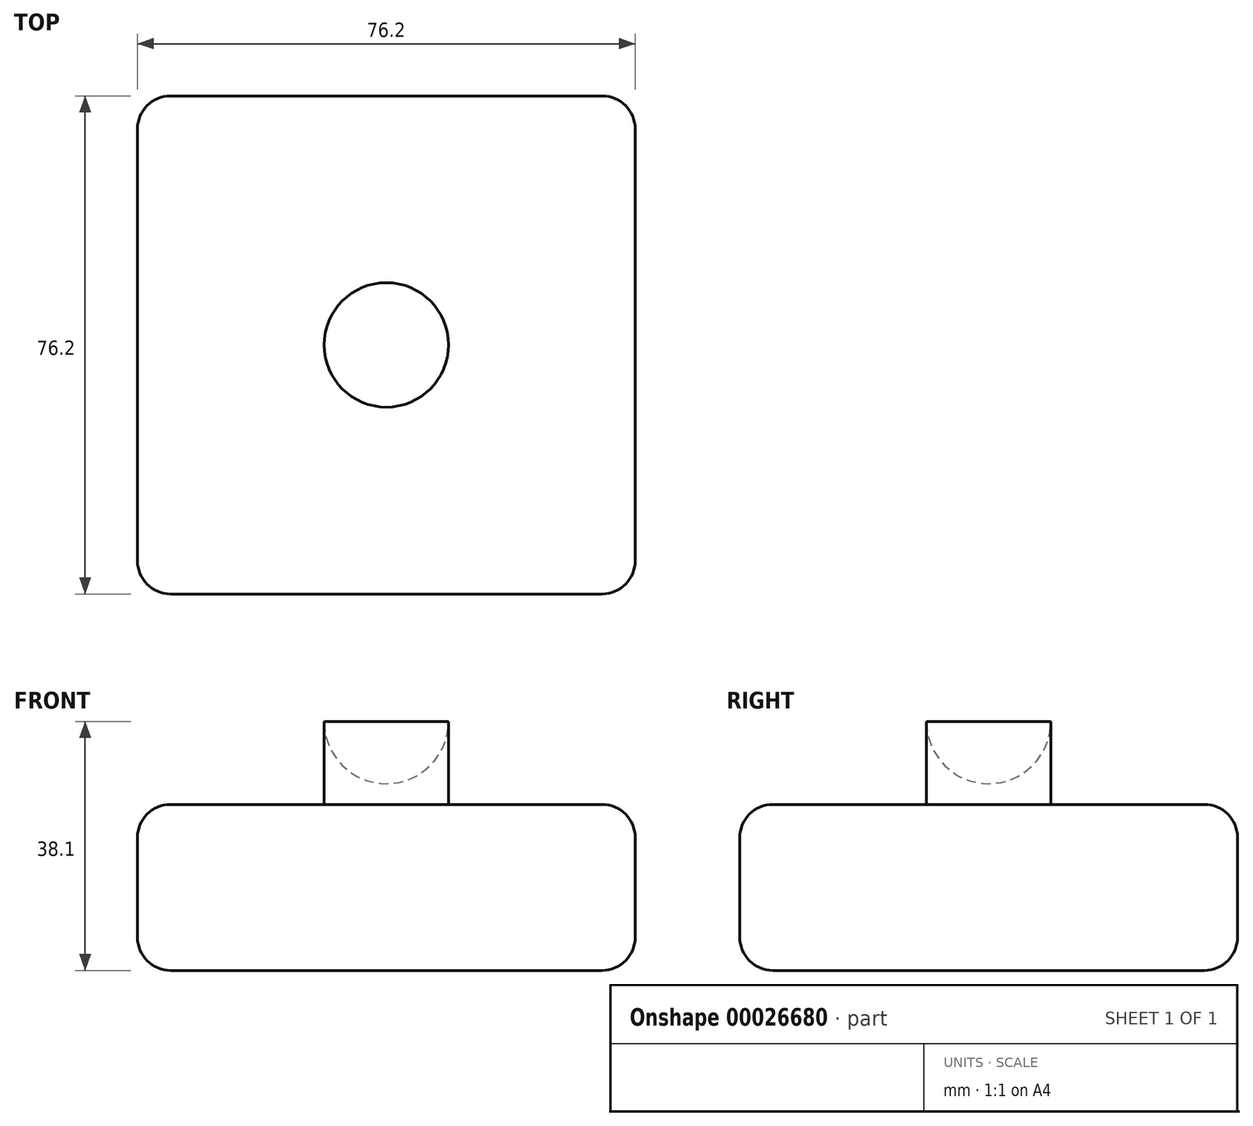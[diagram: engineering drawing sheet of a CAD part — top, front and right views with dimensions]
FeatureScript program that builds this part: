
annotation { "Feature Type Name" : "Feature", "Feature Type Description" : "" }
export const myFeature = defineFeature(function(context is Context, id is Id, definition is map)
    precondition{}
    {
        {
            var Q0;
            Q0=qCreatedBy(makeId("Top.planeOp"),FACE);
            var sketch = newSketch(context, id + "F0", { "sketchPlane" : qUnion([Q0])});
            skLineSegment(sketch, "E0.rect.bottom", {"start": v(-38.1, 38.1) * mm, "end": v(38.1, 38.1) * mm});
            skLineSegment(sketch, "E0.rect.top", {"start": v(-38.1, -38.1) * mm, "end": v(38.1, -38.1) * mm});
            skLineSegment(sketch, "E0.rect.left", {"start": v(-38.1, 38.1) * mm, "end": v(-38.1, -38.1) * mm});
            skLineSegment(sketch, "E0.rect.right", {"start": v(38.1, 38.1) * mm, "end": v(38.1, -38.1) * mm});
            skPoint(sketch, "E0.rect.middle", {"position": v(0, 0) * mm});
            skSolve(sketch);
        }
        {
            var Q0;
            Q0=makeQuery(id+"F0.imprint","IMPRINT",FACE,{"disambiguationData":[TD([[makeQuery(id+"F0.imprint","IMPRINT",EDGE,{"derivedFrom":sQuery(id+"F0.wireOp",EDGE,"E0.rect.bottom")}),-1.0]])]});
            extrude(context, id + "F1", {"entities" : qUnion([Q0]), "depth" : 25.4 * mm});
        }
        {
            var Q0;
            Q0=makeQuery(id+"F1.opExtrude","CAP_EDGE",EDGE,{"disambiguationData":[OSD([sQuery(id+"F0.wireOp",EDGE,"E0.rect.top")])],"isStart":true});
            var Q1;
            Q1=makeQuery(id+"F1.opExtrude","CAP_EDGE",EDGE,{"disambiguationData":[OSD([sQuery(id+"F0.wireOp",EDGE,"E0.rect.right")])],"isStart":true});
            var Q2;
            Q2=makeQuery(id+"F1.opExtrude","CAP_EDGE",EDGE,{"disambiguationData":[OSD([sQuery(id+"F0.wireOp",EDGE,"E0.rect.bottom")])],"isStart":true});
            var Q3;
            Q3=makeQuery(id+"F1.opExtrude","CAP_EDGE",EDGE,{"disambiguationData":[OSD([sQuery(id+"F0.wireOp",EDGE,"E0.rect.left")])],"isStart":true});
            var Q4;
            Q4=makeQuery(id+"F1.opExtrude","CAP_EDGE",EDGE,{"disambiguationData":[OSD([sQuery(id+"F0.wireOp",EDGE,"E0.rect.top")])],"isStart":false});
            var Q5;
            Q5=makeQuery(id+"F1.opExtrude","CAP_EDGE",EDGE,{"disambiguationData":[OSD([sQuery(id+"F0.wireOp",EDGE,"E0.rect.left")])],"isStart":false});
            var Q6;
            Q6=makeQuery(id+"F1.opExtrude","SWEPT_EDGE",EDGE,{"disambiguationData":[OSD([sQuery(id+"F0.wireOp",EDGE,"E0.rect.top"),sQuery(id+"F0.wireOp",EDGE,"E0.rect.left")])]});
            var Q7;
            Q7=makeQuery(id+"F1.opExtrude","SWEPT_EDGE",EDGE,{"disambiguationData":[OSD([sQuery(id+"F0.wireOp",EDGE,"E0.rect.bottom"),sQuery(id+"F0.wireOp",EDGE,"E0.rect.left")])]});
            var Q8;
            Q8=makeQuery(id+"F1.opExtrude","SWEPT_FACE",FACE,{"disambiguationData":[OSD([sQuery(id+"F0.wireOp",EDGE,"E0.rect.bottom")])]});
            var Q9;
            Q9=makeQuery(id+"F1.opExtrude","CAP_EDGE",EDGE,{"disambiguationData":[OSD([sQuery(id+"F0.wireOp",EDGE,"E0.rect.right")])],"isStart":false});
            var Q10;
            Q10=makeQuery(id+"F1.opExtrude","SWEPT_EDGE",EDGE,{"disambiguationData":[OSD([sQuery(id+"F0.wireOp",EDGE,"E0.rect.top"),sQuery(id+"F0.wireOp",EDGE,"E0.rect.right")])]});
            fillet(context, id + "F2", {"entities" : qUnion([Q0, Q1, Q2, Q3, Q4, Q5, Q6, Q7, Q8, Q9, Q10]), "radius" : 5.08 * mm, "tangentPropagation" : true, "allowEdgeOverflow" : false});
        }
        {
            var Q0;
            Q0=makeQuery(id+"F1.opExtrude","CAP_FACE",FACE,{"disambiguationData":[OSD([sQuery(id+"F0.wireOp",EDGE,"E0.rect.bottom"),sQuery(id+"F0.wireOp",EDGE,"E0.rect.top"),sQuery(id+"F0.wireOp",EDGE,"E0.rect.left"),sQuery(id+"F0.wireOp",EDGE,"E0.rect.right")])],"isStart":false});
            var sketch = newSketch(context, id + "F3", { "sketchPlane" : qUnion([Q0])});
            skCircle(sketch, "E1", {"center": v(0, 0) * mm, "radius": 9.53 * mm});
            skSolve(sketch);
        }
        {
            var Q0;
            Q0=makeQuery(id+"F3.imprint","IMPRINT",FACE,{"disambiguationData":[TD([[makeQuery(id+"F3.imprint","IMPRINT",EDGE,{"derivedFrom":sQuery(id+"F3.wireOp",EDGE,"E1")}),1.0]])]});
            extrude(context, id + "F4", {"entities" : qUnion([Q0]), "operationType" : NewBodyOperationType.ADD, "depth" : 12.7 * mm});
        }
        {
            var Q0;
            Q0=makeQuery(id+"F4.opExtrude","CAP_FACE",FACE,{"disambiguationData":[OSD([sQuery(id+"F3.wireOp",EDGE,"E1")])],"isStart":false});
            var sketch = newSketch(context, id + "F5", { "sketchPlane" : qUnion([Q0])});
            skLineSegment(sketch, "E2", {"start": v(0, 9.53) * mm, "end": v(0, -9.53) * mm});
            skSolve(sketch);
        }
        {
            var Q0;
            {var subQ1=sQuery(id+"F5.wireOp",EDGE,"E2");Q0=makeQuery(id+"F5.imprint","IMPRINT",FACE,{"disambiguationData":[TD([[makeQuery(id+"F5.imprint","IMPRINT",EDGE,{"derivedFrom":subQ1}),-1.0]])]});}
            var Q1;
            Q1=sQuery(id+"F5.wireOp",EDGE,"E2");
            revolve(context, id + "F6", {"operationType" : NewBodyOperationType.REMOVE, "entities" : qUnion([Q0]), "axis" : qUnion([Q1]), "revolveType" : RevolveType.FULL, "oppositeDirection" : true});
        }
    });
